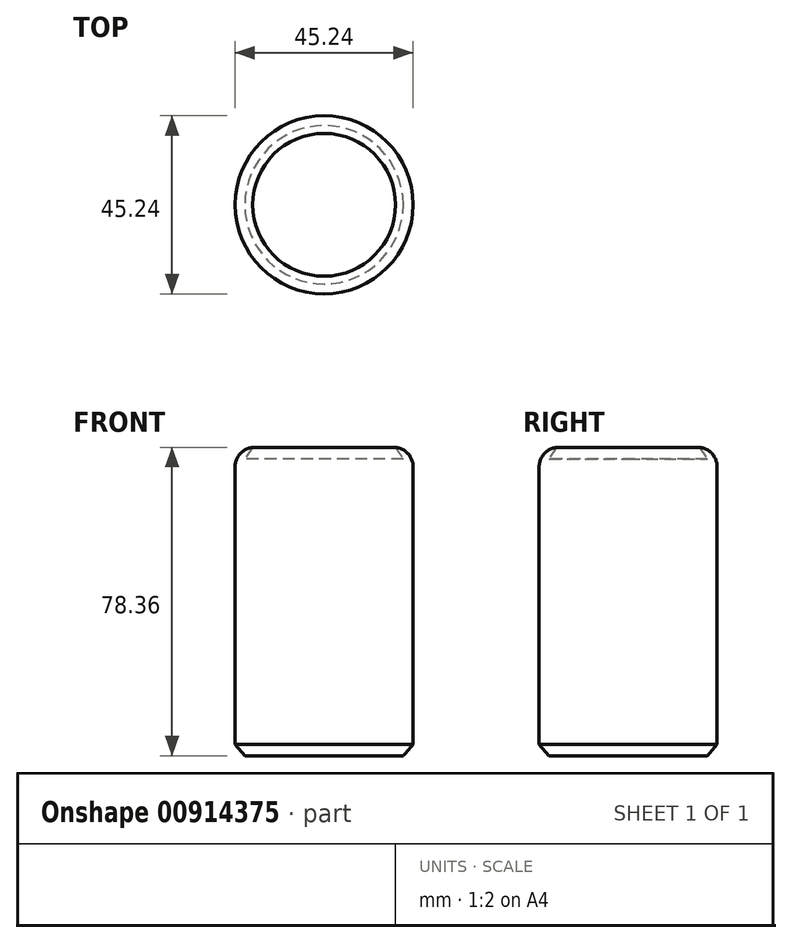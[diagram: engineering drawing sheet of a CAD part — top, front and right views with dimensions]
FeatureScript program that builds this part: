
annotation { "Feature Type Name" : "Feature", "Feature Type Description" : "" }
export const myFeature = defineFeature(function(context is Context, id is Id, definition is map)
    precondition{}
    {
        {
            var Q0;
            Q0=qCreatedBy(makeId("Right.planeOp"),FACE);
            var sketch = newSketch(context, id + "F0", { "sketchPlane" : qUnion([Q0])});
            skLineSegment(sketch, "E0", {"start": v(0, 0) * mm, "end": v(-20.12, 0) * mm});
            skLineSegment(sketch, "E1", {"start": v(-20.12, 0) * mm, "end": v(-22.62, 2.9) * mm});
            skLineSegment(sketch, "E2", {"start": v(-22.62, 2.9) * mm, "end": v(-22.62, 78.36) * mm});
            skLineSegment(sketch, "E3", {"start": v(-22.62, 78.36) * mm, "end": v(-18.14, 78.36) * mm});
            skLineSegment(sketch, "E4", {"start": v(-18.14, 78.36) * mm, "end": v(-20.12, 75.38) * mm});
            skLineSegment(sketch, "E5", {"start": v(-20.12, 75.38) * mm, "end": v(0, 75.38) * mm});
            skLineSegment(sketch, "E6", {"start": v(0, 75.38) * mm, "end": v(0, 0) * mm});
            skSolve(sketch);
        }
        {
            var Q0;
            Q0=makeQuery(id+"F0.imprint","IMPRINT",FACE,{"disambiguationData":[TD([[makeQuery(id+"F0.imprint","IMPRINT",EDGE,{"derivedFrom":sQuery(id+"F0.wireOp",EDGE,"E0")}),-1.0]])]});
            var Q1;
            Q1=sQuery(id+"F0.wireOp",EDGE,"E6");
            revolve(context, id + "F1", {"surfaceOperationType" : NewSurfaceOperationType.NEW, "entities" : qUnion([Q0]), "axis" : qUnion([Q1]), "revolveType" : RevolveType.FULL});
        }
        {
            var Q0;
            Q0=makeQuery(id+"F1.opRevolve","SWEPT_EDGE",EDGE,{"disambiguationData":[OSD([sQuery(id+"F0.wireOp",EDGE,"E2"),sQuery(id+"F0.wireOp",EDGE,"E3")])]});
            fillet(context, id + "F2", {"entities" : qUnion([Q0]), "radius" : 5 * mm, "tangentPropagation" : true, "allowEdgeOverflow" : false});
        }
    });
